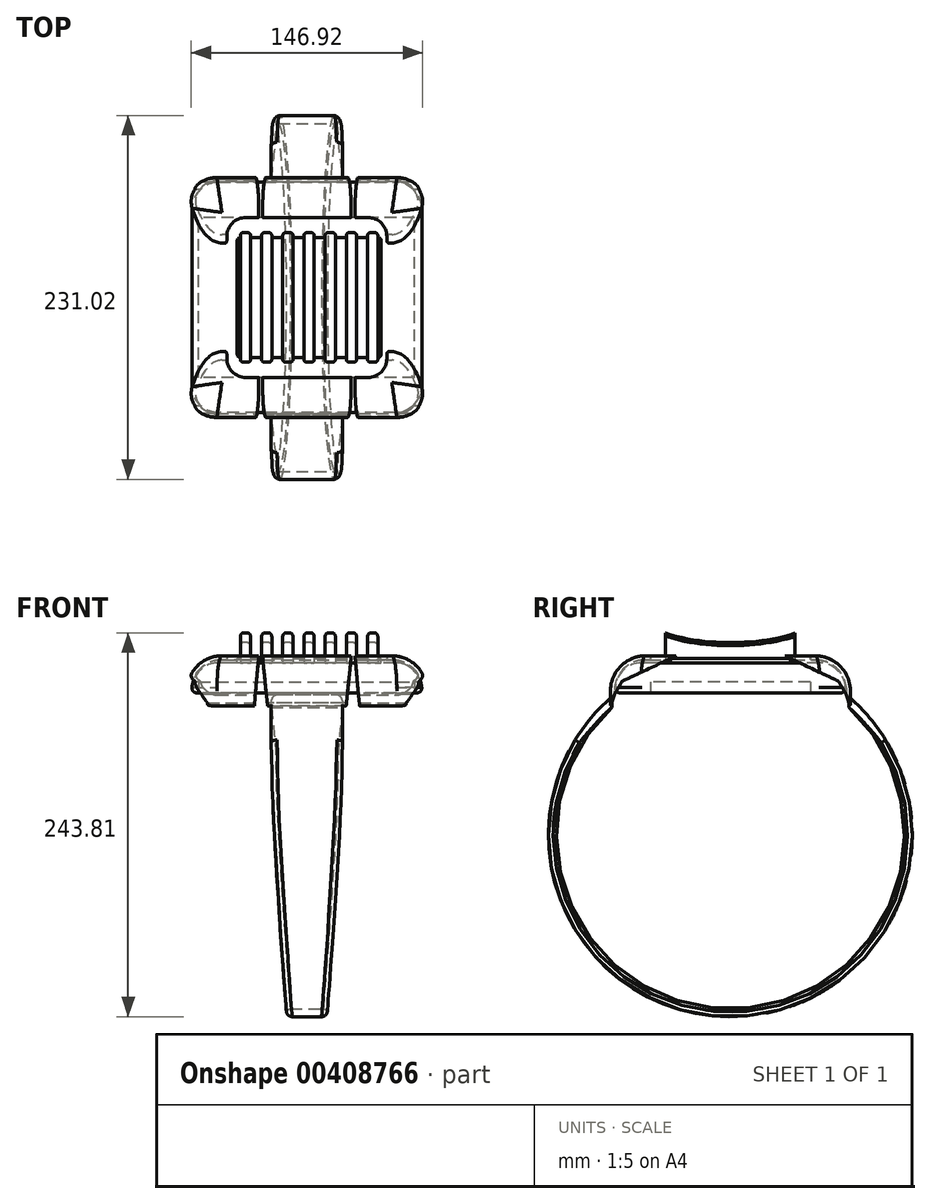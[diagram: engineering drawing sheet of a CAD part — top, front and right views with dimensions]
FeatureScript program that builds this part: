
annotation { "Feature Type Name" : "Feature", "Feature Type Description" : "" }
export const myFeature = defineFeature(function(context is Context, id is Id, definition is map)
    precondition{}
    {
        {
            var Q0;
            Q0=qCreatedBy(makeId("Top.planeOp"),FACE);
            var sketch = newSketch(context, id + "F0", { "sketchPlane" : qUnion([Q0])});
            skLineSegment(sketch, "E0.bottom", {"start": v(-57.15, -76.2) * mm, "end": v(57.15, -76.2) * mm});
            skLineSegment(sketch, "E0.top", {"start": v(-57.15, 76.2) * mm, "end": v(57.15, 76.2) * mm});
            skLineSegment(sketch, "E0.left", {"start": v(-76.2, -57.15) * mm, "end": v(-76.2, 57.15) * mm});
            skLineSegment(sketch, "E0.right", {"start": v(76.2, -57.15) * mm, "end": v(76.2, 57.15) * mm});
            skPoint(sketch, "E0.middle", {"position": v(0, 0) * mm});
            skPoint(sketch, "E1.visualSharp", {"position": v(-76.2, -76.2) * mm});
            skArc(sketch, "E1.filletArc", {"start": v(-76.2, -57.15) * mm, "mid": v(-70.62, -70.62) * mm, "end": v(-57.15, -76.2) * mm});
            skPoint(sketch, "E2.visualSharp", {"position": v(76.2, -76.2) * mm});
            skArc(sketch, "E2.filletArc", {"start": v(57.15, -76.2) * mm, "mid": v(70.62, -70.62) * mm, "end": v(76.2, -57.15) * mm});
            skPoint(sketch, "E3.visualSharp", {"position": v(76.2, 76.2) * mm});
            skArc(sketch, "E3.filletArc", {"start": v(76.2, 57.15) * mm, "mid": v(70.62, 70.62) * mm, "end": v(57.15, 76.2) * mm});
            skPoint(sketch, "E4.visualSharp", {"position": v(-76.2, 76.2) * mm});
            skArc(sketch, "E4.filletArc", {"start": v(-57.15, 76.2) * mm, "mid": v(-70.62, 70.62) * mm, "end": v(-76.2, 57.15) * mm});
            skSolve(sketch);
        }
        {
            var Q0;
            Q0=makeQuery(id+"F0.imprint","IMPRINT",FACE,{"disambiguationData":[TD([[makeQuery(id+"F0.imprint","IMPRINT",EDGE,{"derivedFrom":sQuery(id+"F0.wireOp",EDGE,"E0.bottom")}),1.0]])]});
            extrude(context, id + "F1", {"entities" : qUnion([Q0]), "depth" : 31.75 * mm});
        }
        {
            var Q0;
            Q0=qCreatedBy(makeId("Top.planeOp"),FACE);
            var sketch = newSketch(context, id + "F2", { "sketchPlane" : qUnion([Q0])});
            skLineSegment(sketch, "E5.bottom", {"start": v(-38.73, -50.8) * mm, "end": v(38.74, -50.8) * mm});
            skLineSegment(sketch, "E5.top", {"start": v(-38.73, 50.8) * mm, "end": v(38.74, 50.8) * mm});
            skLineSegment(sketch, "E5.left", {"start": v(-50.8, -38.74) * mm, "end": v(-50.8, 38.74) * mm});
            skLineSegment(sketch, "E5.right", {"start": v(50.8, -38.74) * mm, "end": v(50.8, 38.74) * mm});
            skPoint(sketch, "E5.middle", {"position": v(0, 0) * mm});
            skPoint(sketch, "E6.visualSharp", {"position": v(-50.8, -50.8) * mm});
            skArc(sketch, "E6.filletArc", {"start": v(-50.8, -38.74) * mm, "mid": v(-47.27, -47.27) * mm, "end": v(-38.73, -50.8) * mm});
            skPoint(sketch, "E7.visualSharp", {"position": v(50.8, -50.8) * mm});
            skArc(sketch, "E7.filletArc", {"start": v(38.74, -50.8) * mm, "mid": v(47.27, -47.27) * mm, "end": v(50.8, -38.74) * mm});
            skPoint(sketch, "E8.visualSharp", {"position": v(50.8, 50.8) * mm});
            skArc(sketch, "E8.filletArc", {"start": v(50.8, 38.74) * mm, "mid": v(47.27, 47.27) * mm, "end": v(38.74, 50.8) * mm});
            skPoint(sketch, "E9.visualSharp", {"position": v(-50.8, 50.8) * mm});
            skArc(sketch, "E9.filletArc", {"start": v(-38.73, 50.8) * mm, "mid": v(-47.27, 47.27) * mm, "end": v(-50.8, 38.74) * mm});
            skSolve(sketch);
        }
        {
            var Q0;
            Q0=makeQuery(id+"F1.opExtrude","CAP_EDGE",EDGE,{"disambiguationData":[OSD([sQuery(id+"F0.wireOp",EDGE,"E1.filletArc")])],"isStart":false});
            fillet(context, id + "F3", {"entities" : qUnion([Q0]), "radius" : 22.22 * mm, "tangentPropagation" : true, "allowEdgeOverflow" : false});
        }
        {
            var Q0;
            Q0=makeQuery(id+"F1.opExtrude","CAP_FACE",FACE,{"disambiguationData":[OSD([sQuery(id+"F0.wireOp",EDGE,"E0.bottom"),sQuery(id+"F0.wireOp",EDGE,"E0.top"),sQuery(id+"F0.wireOp",EDGE,"E0.left"),sQuery(id+"F0.wireOp",EDGE,"E0.right"),sQuery(id+"F0.wireOp",EDGE,"E1.filletArc"),sQuery(id+"F0.wireOp",EDGE,"E2.filletArc"),sQuery(id+"F0.wireOp",EDGE,"E3.filletArc"),sQuery(id+"F0.wireOp",EDGE,"E4.filletArc")])],"isStart":true});
            shell(context, id + "F4", {"entities" : qUnion([Q0]), "thickness" : 2.54 * mm});
        }
        {
            var Q0;
            Q0=makeQuery(id+"F2.imprint","IMPRINT",FACE,{"disambiguationData":[TD([[makeQuery(id+"F2.imprint","IMPRINT",EDGE,{"derivedFrom":sQuery(id+"F2.wireOp",EDGE,"E5.bottom")}),1.0]])]});
            extrude(context, id + "F5", {"entities" : qUnion([Q0]), "operationType" : NewBodyOperationType.REMOVE, "depth" : 38.1 * mm});
        }
        {
            var Q0;
            Q0=makeQuery(id+"F5.boolean.opBoolean","INTERSECT",EDGE,{"derivedFrom":[makeQuery(id+"F1.opExtrude","CAP_FACE",FACE,{"disambiguationData":[OSD([sQuery(id+"F0.wireOp",EDGE,"E0.bottom"),sQuery(id+"F0.wireOp",EDGE,"E0.top"),sQuery(id+"F0.wireOp",EDGE,"E0.left"),sQuery(id+"F0.wireOp",EDGE,"E0.right"),sQuery(id+"F0.wireOp",EDGE,"E1.filletArc"),sQuery(id+"F0.wireOp",EDGE,"E2.filletArc"),sQuery(id+"F0.wireOp",EDGE,"E3.filletArc"),sQuery(id+"F0.wireOp",EDGE,"E4.filletArc")])],"isStart":false}),makeQuery(id+"F5.opExtrude","SWEPT_FACE",FACE,{"disambiguationData":[OSD([sQuery(id+"F2.wireOp",EDGE,"E5.left")])]})]});
            var Q1;
            Q1=makeQuery(id+"F5.boolean.opBoolean","INTERSECT",EDGE,{"derivedFrom":[makeQuery(id+"F4.opShell","OFFSET_FACE",FACE,{"disambiguationData":[OSD([sQuery(id+"F0.wireOp",EDGE,"E0.bottom"),sQuery(id+"F0.wireOp",EDGE,"E0.top"),sQuery(id+"F0.wireOp",EDGE,"E0.left"),sQuery(id+"F0.wireOp",EDGE,"E0.right"),sQuery(id+"F0.wireOp",EDGE,"E1.filletArc"),sQuery(id+"F0.wireOp",EDGE,"E2.filletArc"),sQuery(id+"F0.wireOp",EDGE,"E3.filletArc"),sQuery(id+"F0.wireOp",EDGE,"E4.filletArc")])]}),makeQuery(id+"F5.opExtrude","SWEPT_FACE",FACE,{"disambiguationData":[OSD([sQuery(id+"F2.wireOp",EDGE,"E5.left")])]})]});
            var Q2;
            {var subQ0=sQuery(id+"F0.wireOp",EDGE,"E0.right");Q2=makeQuery(id+"F4.opShell","OFFSET_EDGE",EDGE,{"disambiguationData":[OSD([subQ0]),TDD([makeQuery(id+"F1.opExtrude","CAP_EDGE",EDGE,{"disambiguationData":[OSD([subQ0])],"isStart":true})])]});}
            var Q3;
            Q3=makeQuery(id+"F1.opExtrude","SWEPT_FACE",FACE,{"disambiguationData":[OSD([sQuery(id+"F0.wireOp",EDGE,"E0.bottom")])]});
            fillet(context, id + "F6", {"entities" : qUnion([Q0, Q1, Q2, Q3]), "radius" : 0.9 * mm, "tangentPropagation" : true, "allowEdgeOverflow" : false});
        }
        {
            var Q0;
            Q0=qCreatedBy(makeId("Top.planeOp"),FACE);
            var sketch = newSketch(context, id + "F7", { "sketchPlane" : qUnion([Q0])});
            skLineSegment(sketch, "E10", {"start": v(-47.83, 83.07) * mm, "end": v(90.07, -39.95) * mm});
            skSolve(sketch);
        }
        {
            var Q0;
            Q0=qCreatedBy(makeId("Right.planeOp"),FACE);
            var sketch = newSketch(context, id + "F8", { "sketchPlane" : qUnion([Q0])});
            skLineSegment(sketch, "E11", {"start": v(0, -66.48) * mm, "end": v(0, 51.9) * mm, "construction": true});
            skCircle(sketch, "E12", {"center": v(0, -81.93) * mm, "radius": 111.32 * mm});
            skSolve(sketch);
        }
        {
            var Q0;
            Q0=qCreatedBy(makeId("Front.planeOp"),FACE);
            var sketch = newSketch(context, id + "F9", { "sketchPlane" : qUnion([Q0])});
            skLineSegment(sketch, "E13.bottom", {"start": v(-22.77, 28.64) * mm, "end": v(22.77, 28.64) * mm});
            skLineSegment(sketch, "E13.top", {"start": v(-22.77, 33.58) * mm, "end": v(22.77, 33.58) * mm});
            skLineSegment(sketch, "E13.left", {"start": v(-22.77, 28.64) * mm, "end": v(-22.77, 33.58) * mm});
            skLineSegment(sketch, "E13.right", {"start": v(22.77, 28.64) * mm, "end": v(22.77, 33.58) * mm});
            skPoint(sketch, "E13.middle", {"position": v(0, 31.11) * mm});
            skPoint(sketch, "E14.visualSharp", {"position": v(-22.77, 33.58) * mm});
            skLineSegment(sketch, "E14.filletArc", {"start": v(-22.77, 33.58) * mm, "end": v(-22.77, 33.58) * mm});
            skPoint(sketch, "E15.visualSharp", {"position": v(22.77, 33.58) * mm});
            skLineSegment(sketch, "E15.filletArc", {"start": v(22.77, 33.58) * mm, "end": v(22.77, 33.58) * mm});
            skSolve(sketch);
        }
        {
            var Q0;
            Q0=makeQuery(id+"F9.imprint","IMPRINT",FACE,{"disambiguationData":[TD([[makeQuery(id+"F9.imprint","IMPRINT",EDGE,{"derivedFrom":sQuery(id+"F9.wireOp",EDGE,"E13.bottom")}),1.0]])]});
            var Q1;
            Q1=sQuery(id+"F8.wireOp",EDGE,"E12");
            sweep(context, id + "F10", {"profiles" : qUnion([Q0]), "path" : qUnion([Q1])});
        }
        {
            var Q0;
            Q0=qCreatedBy(makeId("Right.planeOp"),FACE);
            var sketch = newSketch(context, id + "F11", { "sketchPlane" : qUnion([Q0])});
            skLineSegment(sketch, "E16", {"start": v(-68.71, 15.6) * mm, "end": v(-73.45, 7.53) * mm});
            skLineSegment(sketch, "E17", {"start": v(-73.45, 7.53) * mm, "end": v(-75.27, 1.85) * mm});
            skLineSegment(sketch, "E18", {"start": v(-75.27, 1.85) * mm, "end": v(-75.27, -1.75) * mm});
            skLineSegment(sketch, "E19.MirrorCS", {"start": v(68.71, 15.6) * mm, "end": v(73.45, 7.53) * mm});
            skLineSegment(sketch, "E20.MirrorCS", {"start": v(73.45, 7.53) * mm, "end": v(75.27, 1.85) * mm});
            skLineSegment(sketch, "E21.MirrorCS", {"start": v(75.27, 1.85) * mm, "end": v(75.27, -1.75) * mm});
            skLineSegment(sketch, "E22", {"start": v(-75.27, -1.75) * mm, "end": v(75.27, -1.75) * mm});
            skLineSegment(sketch, "E23", {"start": v(68.71, 15.6) * mm, "end": v(0.21, 48.05) * mm});
            skLineSegment(sketch, "E24", {"start": v(0.21, 48.05) * mm, "end": v(-68.71, 15.6) * mm});
            skSolve(sketch);
        }
        {
            var Q0;
            Q0 = qSketchRegion(id + "F11", true);
            extrude(context, id + "F12", {"entities" : qUnion([Q0]), "operationType" : NewBodyOperationType.REMOVE, "depth" : 25.4 * mm, "hasSecondDirection" : true, "secondDirectionOppositeDirection" : true, "secondDirectionDepth" : 25.4 * mm});
        }
        {
            var Q0;
            Q0=qCreatedBy(makeId("Front.planeOp"),FACE);
            var sketch = newSketch(context, id + "F13", { "sketchPlane" : qUnion([Q0])});
            skLineSegment(sketch, "E25", {"start": v(29.26, 46.15) * mm, "end": v(51.32, -200.85) * mm});
            skLineSegment(sketch, "E26", {"start": v(51.32, -200.85) * mm, "end": v(12.53, -200.85) * mm});
            skFitSpline(sketch, "E27", {"points": [v(29.26, 46.15) * mm, v(22.88, -22.1) * mm, v(22.14, -49.42) * mm, v(12.53, -200.85) * mm], "startDerivative": vector(-17.07, -248.54) * mm, "endDerivative": vector(-32.92, -420.18) * mm});
            skFitSpline(sketch, "E28.MirrorCS", {"points": [v(-29.26, 46.15) * mm, v(-22.88, -22.1) * mm, v(-22.14, -49.42) * mm, v(-12.53, -200.85) * mm], "startDerivative": vector(17.07, -248.54) * mm, "endDerivative": vector(32.92, -420.18) * mm});
            skLineSegment(sketch, "E29.MirrorCS", {"start": v(-29.26, 46.15) * mm, "end": v(-51.32, -200.85) * mm});
            skLineSegment(sketch, "E30.MirrorCS", {"start": v(-51.32, -200.85) * mm, "end": v(-12.53, -200.85) * mm});
            skSolve(sketch);
        }
        {
            var Q0;
            Q0=makeQuery(id+"F13.imprint","IMPRINT",FACE,{"disambiguationData":[TD([[makeQuery(id+"F13.imprint","IMPRINT",EDGE,{"derivedFrom":sQuery(id+"F13.wireOp",EDGE,"E28.MirrorCS")}),-1.0]])]});
            var Q1;
            Q1=makeQuery(id+"F13.imprint","IMPRINT",FACE,{"disambiguationData":[TD([[makeQuery(id+"F13.imprint","IMPRINT",EDGE,{"derivedFrom":sQuery(id+"F13.wireOp",EDGE,"E25")}),-1.0]])]});
            extrude(context, id + "F14", {"entities" : qUnion([Q0, Q1]), "operationType" : NewBodyOperationType.REMOVE, "oppositeDirection" : true, "depth" : 127 * mm, "hasSecondDirection" : true, "secondDirectionOppositeDirection" : false, "secondDirectionDepth" : 127 * mm});
        }
        {
            var Q0;
            Q0 = qSketchRegion(id + "F11", true);
            extrude(context, id + "F15", {"entities" : qUnion([Q0]), "operationType" : NewBodyOperationType.REMOVE, "oppositeDirection" : true, "depth" : 101.6 * mm, "hasSecondDirection" : true, "secondDirectionOppositeDirection" : false, "secondDirectionDepth" : 76.2 * mm});
        }
        {
            var Q0;
            Q0=makeQuery(id+"F14.boolean.opBoolean","INTERSECT",EDGE,{"derivedFrom":[makeQuery(id+"F10.opSweep","SWEPT_FACE",FACE,{"disambiguationData":[OSD([sQuery(id+"F8.wireOp",EDGE,"E12"),sQuery(id+"F9.wireOp",EDGE,"E13.top")])]}),makeQuery(id+"F14.opExtrude","SWEPT_FACE",FACE,{"disambiguationData":[OSD([sQuery(id+"F13.wireOp",EDGE,"E27")])]})]});
            var Q1;
            {var subQ0=sQuery(id+"F9.wireOp",EDGE,"E13.top");var subQ1=sQuery(id+"F8.wireOp",EDGE,"E12");var subQ2=sQuery(id+"F9.wireOp",EDGE,"E13.right");Q1=makeQuery(id+"F15.boolean.opBoolean","SPLIT",EDGE,{"disambiguationData":[TD([makeQuery(id+"F15.opExtrude","SWEPT_FACE",FACE,{"disambiguationData":[OSD([sQuery(id+"F11.wireOp",EDGE,"E17")])]})])],"derivedFrom":makeQuery(id+"F10.opSweep","SWEPT_EDGE",EDGE,{"disambiguationData":[OSD([subQ1,subQ0,subQ2])]})});}
            var Q2;
            {var subQ0=sQuery(id+"F9.wireOp",EDGE,"E13.top");var subQ1=sQuery(id+"F8.wireOp",EDGE,"E12");var subQ2=sQuery(id+"F9.wireOp",EDGE,"E13.left");Q2=makeQuery(id+"F15.boolean.opBoolean","SPLIT",EDGE,{"disambiguationData":[TD([makeQuery(id+"F15.opExtrude","SWEPT_FACE",FACE,{"disambiguationData":[OSD([sQuery(id+"F11.wireOp",EDGE,"E17")])]})])],"derivedFrom":makeQuery(id+"F10.opSweep","SWEPT_EDGE",EDGE,{"disambiguationData":[OSD([subQ1,subQ0,subQ2])]})});}
            var Q3;
            Q3=makeQuery(id+"F14.boolean.opBoolean","INTERSECT",EDGE,{"derivedFrom":[makeQuery(id+"F10.opSweep","SWEPT_FACE",FACE,{"disambiguationData":[OSD([sQuery(id+"F8.wireOp",EDGE,"E12"),sQuery(id+"F9.wireOp",EDGE,"E13.top")])]}),makeQuery(id+"F14.opExtrude","SWEPT_FACE",FACE,{"disambiguationData":[OSD([sQuery(id+"F13.wireOp",EDGE,"E28.MirrorCS")])]})]});
            var Q4;
            {var subQ0=sQuery(id+"F9.wireOp",EDGE,"E13.top");var subQ1=sQuery(id+"F8.wireOp",EDGE,"E12");var subQ2=sQuery(id+"F9.wireOp",EDGE,"E13.right");Q4=makeQuery(id+"F15.boolean.opBoolean","SPLIT",EDGE,{"disambiguationData":[TD([makeQuery(id+"F15.opExtrude","SWEPT_FACE",FACE,{"disambiguationData":[OSD([sQuery(id+"F11.wireOp",EDGE,"E20.MirrorCS")])]})])],"derivedFrom":makeQuery(id+"F10.opSweep","SWEPT_EDGE",EDGE,{"disambiguationData":[OSD([subQ1,subQ0,subQ2])]})});}
            var Q5;
            {var subQ0=sQuery(id+"F9.wireOp",EDGE,"E13.top");var subQ1=sQuery(id+"F8.wireOp",EDGE,"E12");var subQ2=sQuery(id+"F9.wireOp",EDGE,"E13.left");Q5=makeQuery(id+"F15.boolean.opBoolean","SPLIT",EDGE,{"disambiguationData":[TD([makeQuery(id+"F15.opExtrude","SWEPT_FACE",FACE,{"disambiguationData":[OSD([sQuery(id+"F11.wireOp",EDGE,"E20.MirrorCS")])]})])],"derivedFrom":makeQuery(id+"F10.opSweep","SWEPT_EDGE",EDGE,{"disambiguationData":[OSD([subQ1,subQ0,subQ2])]})});}
            fillet(context, id + "F16", {"entities" : qUnion([Q0, Q1, Q2, Q3, Q4, Q5]), "radius" : 3.68 * mm, "tangentPropagation" : true, "allowEdgeOverflow" : false});
        }
        {
            var Q0;
            Q0=makeQuery(id+"F14.boolean.opBoolean","INTERSECT",EDGE,{"derivedFrom":[makeQuery(id+"F10.opSweep","SWEPT_FACE",FACE,{"disambiguationData":[OSD([sQuery(id+"F8.wireOp",EDGE,"E12"),sQuery(id+"F9.wireOp",EDGE,"E13.bottom")])]}),makeQuery(id+"F14.opExtrude","SWEPT_FACE",FACE,{"disambiguationData":[OSD([sQuery(id+"F13.wireOp",EDGE,"E28.MirrorCS")])]})]});
            var Q1;
            Q1=makeQuery(id+"F14.boolean.opBoolean","INTERSECT",EDGE,{"derivedFrom":[makeQuery(id+"F10.opSweep","SWEPT_FACE",FACE,{"disambiguationData":[OSD([sQuery(id+"F8.wireOp",EDGE,"E12"),sQuery(id+"F9.wireOp",EDGE,"E13.bottom")])]}),makeQuery(id+"F14.opExtrude","SWEPT_FACE",FACE,{"disambiguationData":[OSD([sQuery(id+"F13.wireOp",EDGE,"E27")])]})]});
            fillet(context, id + "F17", {"entities" : qUnion([Q0, Q1]), "radius" : 2.54 * mm, "tangentPropagation" : true, "allowEdgeOverflow" : false});
        }
        {
            var Q0;
            Q0=qCreatedBy(makeId("Right.planeOp"),FACE);
            var sketch = newSketch(context, id + "F18", { "sketchPlane" : qUnion([Q0])});
            skLineSegment(sketch, "E31.bottom", {"start": v(73.2, 27.35) * mm, "end": v(-73.2, 27.35) * mm});
            skLineSegment(sketch, "E31.top", {"start": v(73.2, 8.17) * mm, "end": v(-73.2, 8.17) * mm});
            skLineSegment(sketch, "E31.left", {"start": v(73.2, 27.35) * mm, "end": v(73.2, 8.17) * mm});
            skLineSegment(sketch, "E31.right", {"start": v(-73.2, 27.35) * mm, "end": v(-73.2, 8.17) * mm});
            skPoint(sketch, "E31.middle", {"position": v(0, 17.76) * mm});
            skSolve(sketch);
        }
        {
            var Q0;
            Q0 = qSketchRegion(id + "F18", true);
            extrude(context, id + "F19", {"entities" : qUnion([Q0]), "depth" : 73.02 * mm, "hasSecondDirection" : true, "secondDirectionOppositeDirection" : true, "secondDirectionDepth" : 73.02 * mm});
        }
        {
            var Q0;
            Q0=makeQuery(id+"F19.opExtrude","CAP_EDGE",EDGE,{"disambiguationData":[OSD([sQuery(id+"F18.wireOp",EDGE,"E31.bottom")])],"isStart":false});
            var Q1;
            Q1=makeQuery(id+"F19.opExtrude","SWEPT_EDGE",EDGE,{"disambiguationData":[OSD([sQuery(id+"F18.wireOp",EDGE,"E31.bottom"),sQuery(id+"F18.wireOp",EDGE,"E31.right")])]});
            var Q2;
            Q2=makeQuery(id+"F19.opExtrude","SWEPT_EDGE",EDGE,{"disambiguationData":[OSD([sQuery(id+"F18.wireOp",EDGE,"E31.bottom"),sQuery(id+"F18.wireOp",EDGE,"E31.left")])]});
            var Q3;
            Q3=makeQuery(id+"F19.opExtrude","CAP_EDGE",EDGE,{"disambiguationData":[OSD([sQuery(id+"F18.wireOp",EDGE,"E31.bottom")])],"isStart":true});
            var Q4;
            Q4=makeQuery(id+"F19.opExtrude","CAP_EDGE",EDGE,{"disambiguationData":[OSD([sQuery(id+"F18.wireOp",EDGE,"E31.right")])],"isStart":false});
            var Q5;
            Q5=makeQuery(id+"F19.opExtrude","CAP_EDGE",EDGE,{"disambiguationData":[OSD([sQuery(id+"F18.wireOp",EDGE,"E31.left")])],"isStart":false});
            var Q6;
            Q6=makeQuery(id+"F19.opExtrude","CAP_EDGE",EDGE,{"disambiguationData":[OSD([sQuery(id+"F18.wireOp",EDGE,"E31.left")])],"isStart":true});
            var Q7;
            Q7=makeQuery(id+"F19.opExtrude","CAP_EDGE",EDGE,{"disambiguationData":[OSD([sQuery(id+"F18.wireOp",EDGE,"E31.right")])],"isStart":true});
            fillet(context, id + "F20", {"entities" : qUnion([Q0, Q1, Q2, Q3, Q4, Q5, Q6, Q7]), "radius" : 16.94 * mm, "tangentPropagation" : true, "allowEdgeOverflow" : false});
        }
        {
            var Q0;
            Q0=makeQuery(id+"F19.opExtrude","SWEPT_FACE",FACE,{"disambiguationData":[OSD([sQuery(id+"F18.wireOp",EDGE,"E31.top")])]});
            fillet(context, id + "F21", {"entities" : qUnion([Q0]), "radius" : 3.17 * mm, "tangentPropagation" : true, "allowEdgeOverflow" : false});
        }
        {
            var Q0;
            Q0=qCreatedBy(makeId("Top.planeOp"),FACE);
            var sketch = newSketch(context, id + "F22", { "sketchPlane" : qUnion([Q0])});
            skLineSegment(sketch, "E32.bottom", {"start": v(-35.7, 41.17) * mm, "end": v(-42.27, 41.17) * mm});
            skLineSegment(sketch, "E32.top", {"start": v(-35.7, -41.17) * mm, "end": v(-42.27, -41.17) * mm});
            skLineSegment(sketch, "E32.left", {"start": v(-35.7, 41.17) * mm, "end": v(-35.7, -41.17) * mm});
            skLineSegment(sketch, "E32.right", {"start": v(-42.27, 41.17) * mm, "end": v(-42.27, -41.17) * mm});
            skPoint(sketch, "E32.middle", {"position": v(-39, 0) * mm});
            skLineSegment(sketch, "E33.1.0.0", {"start": v(-28.81, 41.17) * mm, "end": v(-28.81, -41.17) * mm});
            skLineSegment(sketch, "E33.1.0.1", {"start": v(-22.25, 41.17) * mm, "end": v(-22.25, -41.17) * mm});
            skLineSegment(sketch, "E33.1.0.2", {"start": v(-22.25, -41.17) * mm, "end": v(-28.81, -41.17) * mm});
            skLineSegment(sketch, "E33.1.0.3", {"start": v(-22.25, 41.17) * mm, "end": v(-28.81, 41.17) * mm});
            skPoint(sketch, "E33.1.0.4", {"position": v(-25.53, 0) * mm});
            skLineSegment(sketch, "E33.2.0.0", {"start": v(-15.35, 41.17) * mm, "end": v(-15.35, -41.17) * mm});
            skLineSegment(sketch, "E33.2.0.1", {"start": v(-8.78, 41.17) * mm, "end": v(-8.78, -41.17) * mm});
            skLineSegment(sketch, "E33.2.0.2", {"start": v(-8.78, -41.17) * mm, "end": v(-15.35, -41.17) * mm});
            skLineSegment(sketch, "E33.2.0.3", {"start": v(-8.78, 41.17) * mm, "end": v(-15.35, 41.17) * mm});
            skPoint(sketch, "E33.2.0.4", {"position": v(-12.07, 0) * mm});
            skLineSegment(sketch, "E33.3.0.0", {"start": v(-1.89, 41.17) * mm, "end": v(-1.89, -41.17) * mm});
            skLineSegment(sketch, "E33.3.0.1", {"start": v(4.68, 41.17) * mm, "end": v(4.68, -41.17) * mm});
            skLineSegment(sketch, "E33.3.0.2", {"start": v(4.68, -41.17) * mm, "end": v(-1.89, -41.17) * mm});
            skLineSegment(sketch, "E33.3.0.3", {"start": v(4.68, 41.17) * mm, "end": v(-1.89, 41.17) * mm});
            skPoint(sketch, "E33.3.0.4", {"position": v(1.4, 0) * mm});
            skLineSegment(sketch, "E33.4.0.0", {"start": v(11.57, 41.17) * mm, "end": v(11.57, -41.17) * mm});
            skLineSegment(sketch, "E33.4.0.1", {"start": v(18.14, 41.17) * mm, "end": v(18.14, -41.17) * mm});
            skLineSegment(sketch, "E33.4.0.2", {"start": v(18.14, -41.17) * mm, "end": v(11.57, -41.17) * mm});
            skLineSegment(sketch, "E33.4.0.3", {"start": v(18.14, 41.17) * mm, "end": v(11.57, 41.17) * mm});
            skPoint(sketch, "E33.4.0.4", {"position": v(14.86, 0) * mm});
            skLineSegment(sketch, "E33.5.0.0", {"start": v(25.04, 41.17) * mm, "end": v(25.04, -41.17) * mm});
            skLineSegment(sketch, "E33.5.0.1", {"start": v(31.6, 41.17) * mm, "end": v(31.6, -41.17) * mm});
            skLineSegment(sketch, "E33.5.0.2", {"start": v(31.6, -41.17) * mm, "end": v(25.04, -41.17) * mm});
            skLineSegment(sketch, "E33.5.0.3", {"start": v(31.6, 41.17) * mm, "end": v(25.04, 41.17) * mm});
            skPoint(sketch, "E33.5.0.4", {"position": v(28.32, 0) * mm});
            skLineSegment(sketch, "E33.6.0.0", {"start": v(38.5, 41.17) * mm, "end": v(38.5, -41.17) * mm});
            skLineSegment(sketch, "E33.6.0.1", {"start": v(45.06, 41.17) * mm, "end": v(45.06, -41.17) * mm});
            skLineSegment(sketch, "E33.6.0.2", {"start": v(45.06, -41.17) * mm, "end": v(38.5, -41.17) * mm});
            skLineSegment(sketch, "E33.6.0.3", {"start": v(45.06, 41.17) * mm, "end": v(38.5, 41.17) * mm});
            skPoint(sketch, "E33.6.0.4", {"position": v(41.78, 0) * mm});
            skLineSegment(sketch, "E33.direction1", {"start": v(-42.27, -41.17) * mm, "end": v(-28.81, -41.17) * mm, "construction": true});
            skSolve(sketch);
        }
        {
            var Q0;
            Q0=qCreatedBy(makeId("Front.planeOp"),FACE);
            var sketch = newSketch(context, id + "F23", { "sketchPlane" : qUnion([Q0])});
            skLineSegment(sketch, "E34.bottom", {"start": v(-68.73, 15.3) * mm, "end": v(68.4, 15.3) * mm});
            skLineSegment(sketch, "E34.top", {"start": v(-68.73, -19.8) * mm, "end": v(68.4, -19.8) * mm});
            skLineSegment(sketch, "E34.left", {"start": v(-68.73, 15.3) * mm, "end": v(-68.73, -19.8) * mm});
            skLineSegment(sketch, "E34.right", {"start": v(68.4, 15.3) * mm, "end": v(68.4, -19.8) * mm});
            skPoint(sketch, "E34.middle", {"position": v(-0.16, -2.25) * mm});
            skSolve(sketch);
        }
        {
            var Q0;
            Q0=qCreatedBy(makeId("Right.planeOp"),FACE);
            var sketch = newSketch(context, id + "F24", { "sketchPlane" : qUnion([Q0])});
            skEllipse(sketch, "E35", {"center": v(0.18, 57.42) * mm, "majorRadius": 53.87 * mm, "minorRadius": 17.26 * mm, "majorAxis": v(-1, 0)});
            skSolve(sketch);
        }
        {
            var Q0;
            Q0 = qSketchRegion(id + "F22", true);
            extrude(context, id + "F25", {"entities" : qUnion([Q0]), "depth" : 65.53 * mm});
        }
        {
            var Q0;
            Q0=makeQuery(id+"F23.imprint","IMPRINT",FACE,{"disambiguationData":[TD([[makeQuery(id+"F23.imprint","IMPRINT",EDGE,{"derivedFrom":sQuery(id+"F23.wireOp",EDGE,"E34.bottom")}),-1.0]])]});
            extrude(context, id + "F26", {"entities" : qUnion([Q0]), "operationType" : NewBodyOperationType.REMOVE, "oppositeDirection" : true, "depth" : 50.8 * mm, "hasSecondDirection" : true, "secondDirectionOppositeDirection" : false, "secondDirectionDepth" : 50.8 * mm});
        }
        {
            var Q0;
            Q0=makeQuery(id+"F24.imprint","IMPRINT",FACE,{"disambiguationData":[TD([[makeQuery(id+"F24.imprint","IMPRINT",EDGE,{"derivedFrom":sQuery(id+"F24.wireOp",EDGE,"E35")}),1.0]])]});
            extrude(context, id + "F27", {"entities" : qUnion([Q0]), "operationType" : NewBodyOperationType.REMOVE, "oppositeDirection" : true, "depth" : 50.8 * mm, "hasSecondDirection" : true, "secondDirectionOppositeDirection" : false, "secondDirectionDepth" : 50.8 * mm});
        }
        {
            var Q0;
            Q0=makeQuery(id+"F25.opExtrude","SWEPT_FACE",FACE,{"disambiguationData":[OSD([sQuery(id+"F22.wireOp",EDGE,"E33.6.0.1")])]});
            var Q1;
            Q1=makeQuery(id+"F25.opExtrude","SWEPT_FACE",FACE,{"disambiguationData":[OSD([sQuery(id+"F22.wireOp",EDGE,"E33.5.0.1")])]});
            var Q2;
            Q2=makeQuery(id+"F25.opExtrude","SWEPT_FACE",FACE,{"disambiguationData":[OSD([sQuery(id+"F22.wireOp",EDGE,"E33.4.0.1")])]});
            var Q3;
            Q3=makeQuery(id+"F25.opExtrude","SWEPT_FACE",FACE,{"disambiguationData":[OSD([sQuery(id+"F22.wireOp",EDGE,"E33.3.0.1")])]});
            var Q4;
            Q4=makeQuery(id+"F25.opExtrude","SWEPT_FACE",FACE,{"disambiguationData":[OSD([sQuery(id+"F22.wireOp",EDGE,"E33.2.0.1")])]});
            var Q5;
            Q5=makeQuery(id+"F25.opExtrude","SWEPT_FACE",FACE,{"disambiguationData":[OSD([sQuery(id+"F22.wireOp",EDGE,"E33.1.0.1")])]});
            var Q6;
            Q6=makeQuery(id+"F25.opExtrude","SWEPT_FACE",FACE,{"disambiguationData":[OSD([sQuery(id+"F22.wireOp",EDGE,"E32.left")])]});
            var Q7;
            Q7=makeQuery(id+"F25.opExtrude","SWEPT_FACE",FACE,{"disambiguationData":[OSD([sQuery(id+"F22.wireOp",EDGE,"E33.6.0.0")])]});
            var Q8;
            Q8=makeQuery(id+"F25.opExtrude","SWEPT_FACE",FACE,{"disambiguationData":[OSD([sQuery(id+"F22.wireOp",EDGE,"E33.5.0.0")])]});
            var Q9;
            Q9=makeQuery(id+"F25.opExtrude","SWEPT_FACE",FACE,{"disambiguationData":[OSD([sQuery(id+"F22.wireOp",EDGE,"E33.4.0.0")])]});
            var Q10;
            Q10=makeQuery(id+"F25.opExtrude","SWEPT_FACE",FACE,{"disambiguationData":[OSD([sQuery(id+"F22.wireOp",EDGE,"E33.3.0.0")])]});
            var Q11;
            Q11=makeQuery(id+"F25.opExtrude","SWEPT_FACE",FACE,{"disambiguationData":[OSD([sQuery(id+"F22.wireOp",EDGE,"E33.2.0.0")])]});
            var Q12;
            Q12=makeQuery(id+"F25.opExtrude","SWEPT_FACE",FACE,{"disambiguationData":[OSD([sQuery(id+"F22.wireOp",EDGE,"E33.1.0.0")])]});
            var Q13;
            Q13=makeQuery(id+"F25.opExtrude","SWEPT_FACE",FACE,{"disambiguationData":[OSD([sQuery(id+"F22.wireOp",EDGE,"E32.right")])]});
            fillet(context, id + "F28", {"entities" : qUnion([Q0, Q1, Q2, Q3, Q4, Q5, Q6, Q7, Q8, Q9, Q10, Q11, Q12, Q13]), "radius" : 1.9 * mm, "tangentPropagation" : true, "allowEdgeOverflow" : false});
        }
        {
            var Q0;
            Q0=qCreatedBy(makeId("Front.planeOp"),FACE);
            var sketch = newSketch(context, id + "F29", { "sketchPlane" : qUnion([Q0])});
            skLineSegment(sketch, "E36.bottom", {"start": v(-44.2, 25.72) * mm, "end": v(47.17, 25.72) * mm});
            skLineSegment(sketch, "E36.top", {"start": v(-44.2, 29.95) * mm, "end": v(47.17, 29.95) * mm});
            skLineSegment(sketch, "E36.left", {"start": v(-44.2, 25.72) * mm, "end": v(-44.2, 29.95) * mm});
            skLineSegment(sketch, "E36.right", {"start": v(47.17, 25.72) * mm, "end": v(47.17, 29.95) * mm});
            skPoint(sketch, "E36.middle", {"position": v(1.49, 27.84) * mm});
            skSolve(sketch);
        }
        {
            var Q0;
            Q0 = qSketchRegion(id + "F29", true);
            extrude(context, id + "F30", {"entities" : qUnion([Q0]), "operationType" : NewBodyOperationType.ADD, "depth" : 38.1 * mm, "hasSecondDirection" : true, "secondDirectionOppositeDirection" : true, "secondDirectionDepth" : 38.1 * mm});
        }
        {
            var Q0;
            Q0=makeQuery(id+"F30.opExtrude","CAP_EDGE",EDGE,{"disambiguationData":[OSD([sQuery(id+"F29.wireOp",EDGE,"E36.left")])],"isStart":false});
            var Q1;
            Q1=makeQuery(id+"F30.opExtrude","CAP_EDGE",EDGE,{"disambiguationData":[OSD([sQuery(id+"F29.wireOp",EDGE,"E36.right")])],"isStart":false});
            var Q2;
            Q2=makeQuery(id+"F30.opExtrude","CAP_EDGE",EDGE,{"disambiguationData":[OSD([sQuery(id+"F29.wireOp",EDGE,"E36.right")])],"isStart":true});
            var Q3;
            Q3=makeQuery(id+"F30.opExtrude","CAP_EDGE",EDGE,{"disambiguationData":[OSD([sQuery(id+"F29.wireOp",EDGE,"E36.left")])],"isStart":true});
            fillet(context, id + "F31", {"entities" : qUnion([Q0, Q1, Q2, Q3]), "radius" : 1.9 * mm, "tangentPropagation" : true, "allowEdgeOverflow" : false});
        }
    });
